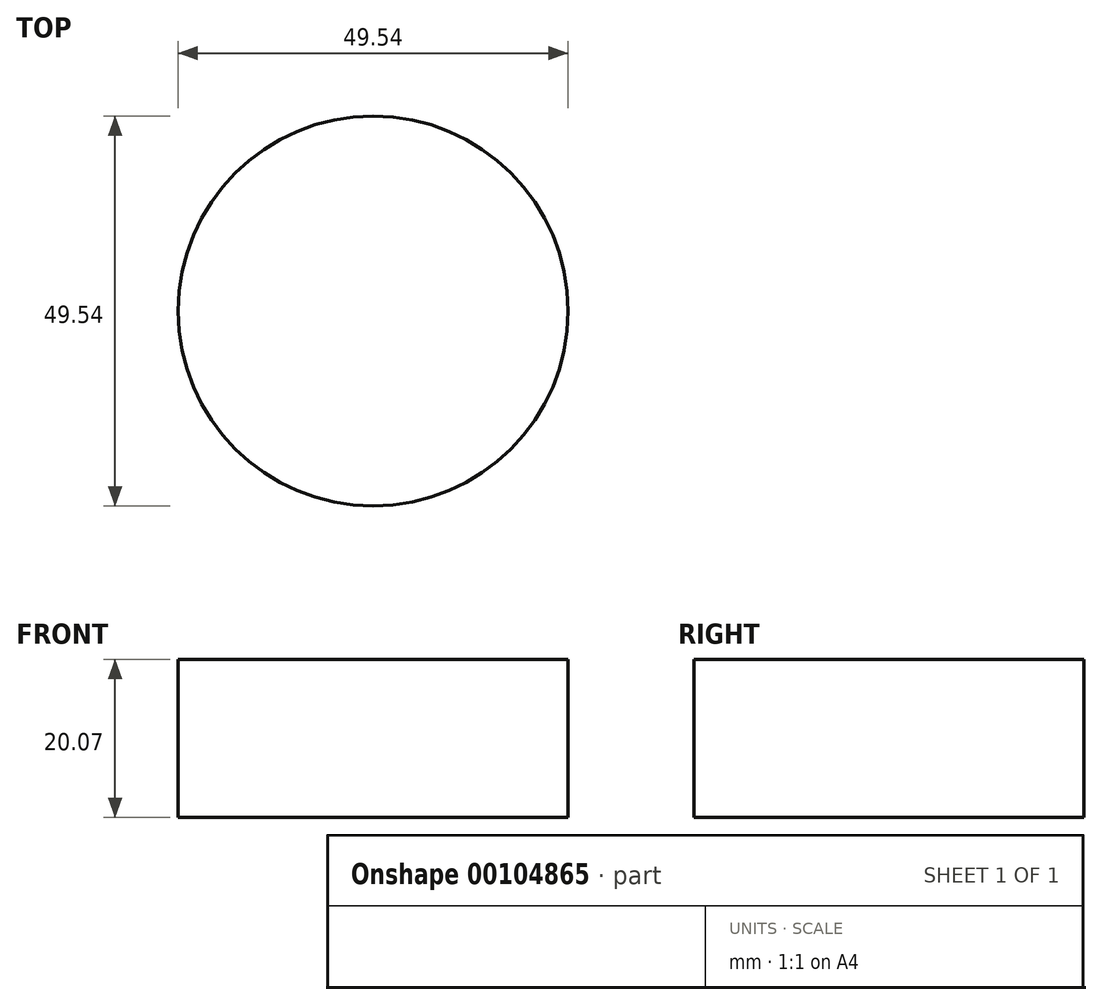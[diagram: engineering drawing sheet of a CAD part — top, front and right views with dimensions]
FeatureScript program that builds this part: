
annotation { "Feature Type Name" : "Feature", "Feature Type Description" : "" }
export const myFeature = defineFeature(function(context is Context, id is Id, definition is map)
    precondition{}
    {
        {
            var Q0;
            Q0=qCreatedBy(makeId("Top.planeOp"),FACE);
            var sketch = newSketch(context, id + "F0", { "sketchPlane" : qUnion([Q0])});
            skCircle(sketch, "E0", {"center": v(0, 0) * mm, "radius": 24.77 * mm});
            skSolve(sketch);
        }
        {
            var Q0;
            Q0=makeQuery(id+"F0.imprint","IMPRINT",FACE,{"disambiguationData":[TD([[makeQuery(id+"F0.imprint","IMPRINT",EDGE,{"derivedFrom":sQuery(id+"F0.wireOp",EDGE,"E0")}),1.0]])]});
            extrude(context, id + "F1", {"entities" : qUnion([Q0]), "depth" : 20.07 * mm});
        }
    });
